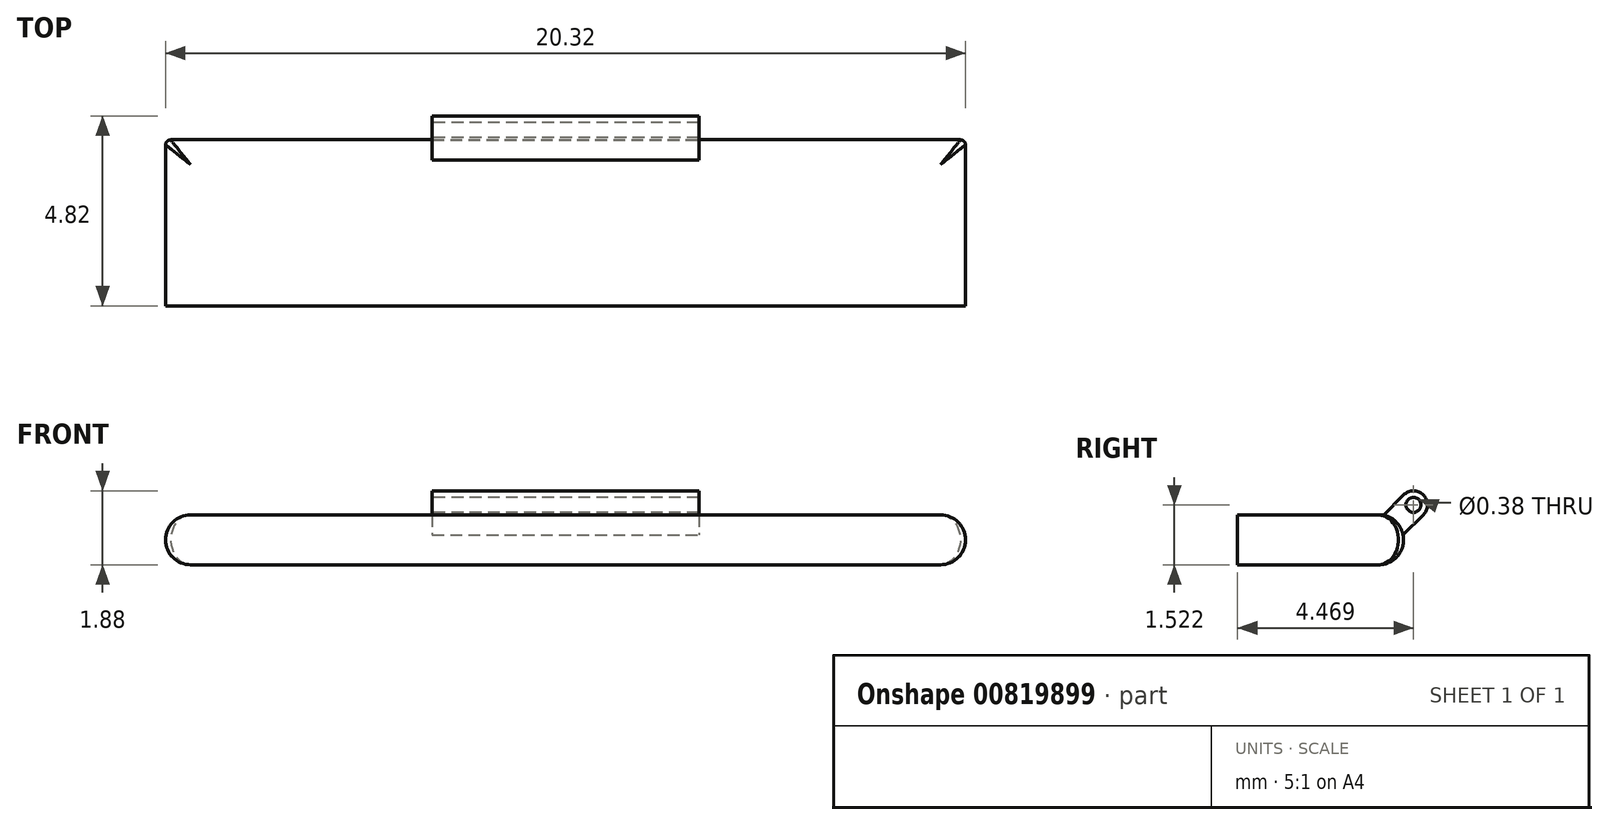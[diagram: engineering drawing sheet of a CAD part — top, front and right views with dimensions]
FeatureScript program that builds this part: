
annotation { "Feature Type Name" : "Feature", "Feature Type Description" : "" }
export const myFeature = defineFeature(function(context is Context, id is Id, definition is map)
    precondition{}
    {
        {
            var Q0;
            Q0=qCreatedBy(makeId("Top.planeOp"),FACE);
            var sketch = newSketch(context, id + "F0", { "sketchPlane" : qUnion([Q0])});
            skLineSegment(sketch, "E0.bottom", {"start": v(0, 0) * mm, "end": v(20.32, 0) * mm});
            skLineSegment(sketch, "E0.top", {"start": v(0, 8.46) * mm, "end": v(20.32, 8.46) * mm});
            skLineSegment(sketch, "E0.left", {"start": v(0, 0) * mm, "end": v(0, 8.46) * mm});
            skLineSegment(sketch, "E0.right", {"start": v(20.32, 0) * mm, "end": v(20.32, 8.46) * mm});
            skSolve(sketch);
        }
        {
            var Q0;
            Q0=qSketchRegion(id+"F0",true);
            extrude(context, id + "F1", {"entities" : qUnion([Q0]), "depth" : 1.27 * mm, "offsetDistance" : 25.4 * mm});
        }
        {
            var Q0;
            Q0=qCreatedBy(makeId("Right.planeOp"),FACE);
            var sketch = newSketch(context, id + "F2", { "sketchPlane" : qUnion([Q0])});
            skLineSegment(sketch, "E1", {"start": v(0, 1.27) * mm, "end": v(-0.25, 1.52) * mm});
            skCircle(sketch, "E2", {"center": v(-0.25, 1.52) * mm, "radius": 0.36 * mm});
            skLineSegment(sketch, "E3.0", {"start": v(0, 1.27) * mm, "end": v(8.46, 1.27) * mm});
            skLineSegment(sketch, "E4.0", {"start": v(0, 1.27) * mm, "end": v(0, 0) * mm});
            skLineSegment(sketch, "E5", {"start": v(-0.25, 1.52) * mm, "end": v(-0.5, 1.27) * mm});
            skLineSegment(sketch, "E6", {"start": v(-0.25, 1.52) * mm, "end": v(0, 1.78) * mm});
            skLineSegment(sketch, "E7", {"start": v(0, 1.78) * mm, "end": v(0.5, 1.27) * mm});
            skLineSegment(sketch, "E8", {"start": v(-0.5, 1.27) * mm, "end": v(0, 0.77) * mm});
            skSolve(sketch);
        }
        {
            var Q0;
            Q0=qSketchRegion(id+"F2",true);
            extrude(context, id + "F3", {"entities" : qUnion([Q0]), "operationType" : NewBodyOperationType.ADD, "depth" : 6.77 * mm, "offsetDistance" : 25.4 * mm});
        }
        {
            var Q0;
            Q0=makeQuery(id+"F3.boolean.opBoolean","MERGE",FACE,{"derivedFrom":[makeQuery(id+"F1.opExtrude","SWEPT_FACE",FACE,{"disambiguationData":[OSD([sQuery(id+"F0.wireOp",EDGE,"E0.left")])]}),makeQuery(id+"F3.opExtrude","CAP_FACE",FACE,{"disambiguationData":[OSD([sQuery(id+"F2.wireOp",EDGE,"E2"),sQuery(id+"F2.wireOp",EDGE,"E3.0"),sQuery(id+"F2.wireOp",EDGE,"E4.0"),sQuery(id+"F2.wireOp",EDGE,"E7"),sQuery(id+"F2.wireOp",EDGE,"E8")])],"isStart":true})]});
            cPlane(context, id + "F4", {"entities" : qUnion([Q0]), "cplaneType" : CPlaneType.OFFSET, "offset" : 10.16 * mm, "oppositeDirection" : true, "width" : 152.4 * mm, "height" : 152.4 * mm});
        }
        {
            var Q0;
            Q0=qCreatedBy(id+"F4.planeOp",FACE);
            var sketch = newSketch(context, id + "F5", { "sketchPlane" : qUnion([Q0])});
            skLineSegment(sketch, "E9.0", {"start": v(-0.5, 1.27) * mm, "end": v(-8.46, 1.27) * mm});
            skLineSegment(sketch, "E10.0", {"start": v(-8.46, 1.27) * mm, "end": v(-8.46, 0) * mm});
            skLineSegment(sketch, "E11", {"start": v(-8.46, 1.27) * mm, "end": v(-8.7, 1.52) * mm});
            skCircle(sketch, "E12", {"center": v(-8.7, 1.52) * mm, "radius": 0.36 * mm});
            skLineSegment(sketch, "E13", {"start": v(-8.7, 1.52) * mm, "end": v(-8.46, 1.77) * mm});
            skLineSegment(sketch, "E14", {"start": v(-8.46, 1.77) * mm, "end": v(-7.96, 1.27) * mm});
            skLineSegment(sketch, "E15", {"start": v(-8.7, 1.52) * mm, "end": v(-8.96, 1.27) * mm});
            skLineSegment(sketch, "E16", {"start": v(-8.96, 1.27) * mm, "end": v(-8.46, 0.77) * mm});
            skSolve(sketch);
        }
        {
            var Q0;
            Q0=qSketchRegion(id+"F5",true);
            extrude(context, id + "F6", {"entities" : qUnion([Q0]), "operationType" : NewBodyOperationType.ADD, "depth" : 3.4 * mm, "offsetDistance" : 25.4 * mm, "hasSecondDirection" : true, "secondDirectionOppositeDirection" : true, "secondDirectionDepth" : 3.4 * mm});
        }
        {
            var Q0;
            Q0=makeQuery(id+"F6.opExtrude","CAP_FACE",FACE,{"disambiguationData":[OSD([sQuery(id+"F5.wireOp",EDGE,"E9.0"),sQuery(id+"F5.wireOp",EDGE,"E10.0"),sQuery(id+"F5.wireOp",EDGE,"E12"),sQuery(id+"F5.wireOp",EDGE,"E14"),sQuery(id+"F5.wireOp",EDGE,"E16")])],"isStart":false});
            var sketch = newSketch(context, id + "F7", { "sketchPlane" : qUnion([Q0])});
            skCircle(sketch, "E17", {"center": v(-8.7, 1.52) * mm, "radius": 0.2 * mm});
            skArc(sketch, "E18.0", {"start": v(0, 1.78) * mm, "mid": v(0.5, 1.78) * mm, "end": v(0.5, 1.27) * mm});
            skCircle(sketch, "E19", {"center": v(0.25, 1.52) * mm, "radius": 0.2 * mm});
            skSolve(sketch);
        }
        {
            var Q0;
            Q0=qSketchRegion(id+"F7",true);
            extrude(context, id + "F8", {"entities" : qUnion([Q0]), "operationType" : NewBodyOperationType.REMOVE, "oppositeDirection" : true, "depth" : 25.4 * mm, "offsetDistance" : 25.4 * mm, "hasSecondDirection" : true, "secondDirectionOppositeDirection" : false, "secondDirectionDepth" : 25.4 * mm});
        }
        {
            var Q0;
            Q0=makeQuery(id+"F1.opExtrude","CAP_EDGE",EDGE,{"disambiguationData":[OSD([sQuery(id+"F0.wireOp",EDGE,"E0.bottom")])],"isStart":true});
            var Q1;
            Q1=makeQuery(id+"F1.opExtrude","CAP_EDGE",EDGE,{"disambiguationData":[OSD([sQuery(id+"F0.wireOp",EDGE,"E0.top")])],"isStart":true});
            var Q2;
            {var subQ0=sQuery(id+"F0.wireOp",EDGE,"E0.left");var subQ1=sQuery(id+"F0.wireOp",EDGE,"E0.top");Q2=makeQuery(id+"F6.boolean.opBoolean","SPLIT",EDGE,{"disambiguationData":[TD([makeQuery(id+"F1.opExtrude","SWEPT_FACE",FACE,{"disambiguationData":[OSD([subQ0])]})])],"derivedFrom":makeQuery(id+"F1.opExtrude","CAP_EDGE",EDGE,{"disambiguationData":[OSD([subQ1])],"isStart":false})});}
            var Q3;
            Q3=makeQuery(id+"F1.opExtrude","CAP_EDGE",EDGE,{"disambiguationData":[OSD([sQuery(id+"F0.wireOp",EDGE,"E0.left")])],"isStart":false});
            var Q4;
            Q4=makeQuery(id+"F1.opExtrude","CAP_EDGE",EDGE,{"disambiguationData":[OSD([sQuery(id+"F0.wireOp",EDGE,"E0.left")])],"isStart":true});
            var Q5;
            Q5=makeQuery(id+"F1.opExtrude","CAP_EDGE",EDGE,{"disambiguationData":[OSD([sQuery(id+"F0.wireOp",EDGE,"E0.right")])],"isStart":false});
            var Q6;
            Q6=makeQuery(id+"F1.opExtrude","CAP_EDGE",EDGE,{"disambiguationData":[OSD([sQuery(id+"F0.wireOp",EDGE,"E0.right")])],"isStart":true});
            fillet(context, id + "F9", {"entities" : qUnion([Q0, Q1, Q2, Q3, Q4, Q5, Q6]), "radius" : 0.64 * mm, "tangentPropagation" : true, "allowEdgeOverflow" : false});
        }
        {
            var Q0;
            Q0=makeQuery(id+"F9.opFillet","BLEND_EDGE",EDGE,{"blendedFrom":[makeQuery(id+"F1.opExtrude","CAP_EDGE",EDGE,{"disambiguationData":[OSD([sQuery(id+"F0.wireOp",EDGE,"E0.bottom")])],"isStart":true}),makeQuery(id+"F1.opExtrude","CAP_EDGE",EDGE,{"disambiguationData":[OSD([sQuery(id+"F0.wireOp",EDGE,"E0.left")])],"isStart":true})],"blendedInto":[]});
            var Q1;
            Q1=makeQuery(id+"F9.opFillet","BLEND_EDGE",EDGE,{"blendedFrom":[makeQuery(id+"F1.opExtrude","CAP_EDGE",EDGE,{"disambiguationData":[OSD([sQuery(id+"F0.wireOp",EDGE,"E0.bottom")])],"isStart":true}),makeQuery(id+"F1.opExtrude","CAP_EDGE",EDGE,{"disambiguationData":[OSD([sQuery(id+"F0.wireOp",EDGE,"E0.right")])],"isStart":true})],"blendedInto":[]});
            var Q2;
            Q2=makeQuery(id+"F9.opFillet","BLEND_EDGE",EDGE,{"blendedFrom":[makeQuery(id+"F1.opExtrude","CAP_EDGE",EDGE,{"disambiguationData":[OSD([sQuery(id+"F0.wireOp",EDGE,"E0.top")])],"isStart":true}),makeQuery(id+"F1.opExtrude","CAP_EDGE",EDGE,{"disambiguationData":[OSD([sQuery(id+"F0.wireOp",EDGE,"E0.right")])],"isStart":true})],"blendedInto":[]});
            var Q3;
            Q3=makeQuery(id+"F9.opFillet","BLEND_EDGE",EDGE,{"blendedFrom":[makeQuery(id+"F1.opExtrude","CAP_EDGE",EDGE,{"disambiguationData":[OSD([sQuery(id+"F0.wireOp",EDGE,"E0.top")])],"isStart":true}),makeQuery(id+"F1.opExtrude","CAP_EDGE",EDGE,{"disambiguationData":[OSD([sQuery(id+"F0.wireOp",EDGE,"E0.left")])],"isStart":true})],"blendedInto":[]});
            fillet(context, id + "F10", {"entities" : qUnion([Q0, Q1, Q2, Q3]), "radius" : 0.13 * mm, "tangentPropagation" : true, "allowEdgeOverflow" : false});
        }
        {
            var Q0;
            Q0=qCreatedBy(id+"F4.planeOp",FACE);
            var sketch = newSketch(context, id + "F11", { "sketchPlane" : qUnion([Q0])});
            skLineSegment(sketch, "E20.bottom", {"start": v(-4.24, 0) * mm, "end": v(1.88, 0) * mm});
            skLineSegment(sketch, "E20.top", {"start": v(-4.24, 3.48) * mm, "end": v(1.88, 3.48) * mm});
            skLineSegment(sketch, "E20.left", {"start": v(-4.24, 0) * mm, "end": v(-4.24, 3.48) * mm});
            skLineSegment(sketch, "E20.right", {"start": v(1.88, 0) * mm, "end": v(1.88, 3.48) * mm});
            skSolve(sketch);
        }
        {
            var Q0;
            Q0 = qSketchRegion(id + "F11", true);
            extrude(context, id + "F12", {"entities" : qUnion([Q0]), "operationType" : NewBodyOperationType.REMOVE, "oppositeDirection" : true, "depth" : 25.4 * mm, "offsetDistance" : 25.4 * mm, "hasSecondDirection" : true, "secondDirectionOppositeDirection" : false, "secondDirectionDepth" : 25.4 * mm});
        }
    });
